# Revit family: Grinder_Pump-Single_Seal-Zoeller-818_819_820_Non_Automatic_Series
name_source: partatom
category: Mechanical Equipment
units: mm (PartAtom-declared; Revit-internal decimal feet)

## family parameters
Always vertical = No
Cut with Voids When Loaded = No
OmniClass Number = 23.60.30.21
OmniClass Title = Pumps
Part Type = Normal
Room Calculation Point = No
Round Connector Dimension = Use Radius
Shared = Yes
Work Plane-Based = Yes

## types (5) — shared parameters
Adapter = Cast Iron
Assembly Code = D2090
Auto On/Off Points = Variable level float switch, customer sets
Cap = Cast Iron
Cooling = Oil filled
Cord Length = 240"
Cord Type = SOW or SOOW multi-wire neoprene
Cutter = Type 440C stainless steel hardened to a Rockwell C55-60
Default Elevation = 0"
Description = Shark Grinder Single Seal Pump With Integral Control.
Discharge Diameter = 1 1/4"
Discharge Radius = 5/8"
Hardware = Stainless Steel
Height = 18 5/8"
Hertz = 60
Impeller = Engineered plastic
Impeller Type = Vortex
Installation Type = Floor Mounted
Insulation = Class B
Length = 8"
Lower Bearing = Ball bearing
Manufacturer = Zoeller
Material = Cast Iron-Zoeller-Powder Coated Epoxy
Max. Operating Temp. = 130°F (54°C)
Mechanical Seals = Carbon/Ceramic
Motor Housing = Cast Iron
Motor Protection = Auto reset thermal overload
Motor Shaft = Stainless Steel
Nominal Height = 5"
O-Ring Seals = Neoprene
Operation = Non-Automatic
Phase = 1
Price = Prices may vary. Please consult Manufacturer Representative for most up-to-date price list.
Product Documentation Link = http://cdn.qleapahead.com
Product Page URL = http://www.zoellerpumps.com
Pump Housing = Cast Iron
RPM = 3450
Shipping Weight = 88 lbs.
Type = Capacitor Start/Run
URL = http://www.zoellerengprod.com
Upper Bearing = Ball Bearing
Warranty Information = 36 Months (Limited)
Waste Connection = Yes
Width = 11 5/8"

## per-type parameters (varying)
| type | Amps | Apparent Load | Flow @ 5' | Max. Head | Model | Motor | Voltage |
| E820 - 230V/1Ph/13.7A/2HP | 14 A | 3151 VA | 46 GPM | 1284" | E820 | 2 HP | 230 V |
| I820 - 200V/1Ph/15.5A/2HP | 16 A | 3100 VA | 46 GPM | 1284" | I820 | 2 HP | 200 V |
| N818 - 115V/1Ph/13.6A/1HP | 14 A | 1564 VA | 43 GPM | 636" | N818 | 1 HP | 115 V |
| I819 - 200V/1Ph/12A/1.5HP | 12 A | 2400 VA | 43 GPM | 972" | I819 | 1.5 HP | 200 V |
| E819 - 230V/1Ph/15.5A/1.5HP | 16 A | 3565 VA | 43 GPM | 972" | E819 | 1.5 HP | 230 V |

## geometry (parser evidence)
native form markers: Sweep x2
no freeform markers — native parametric forms only
